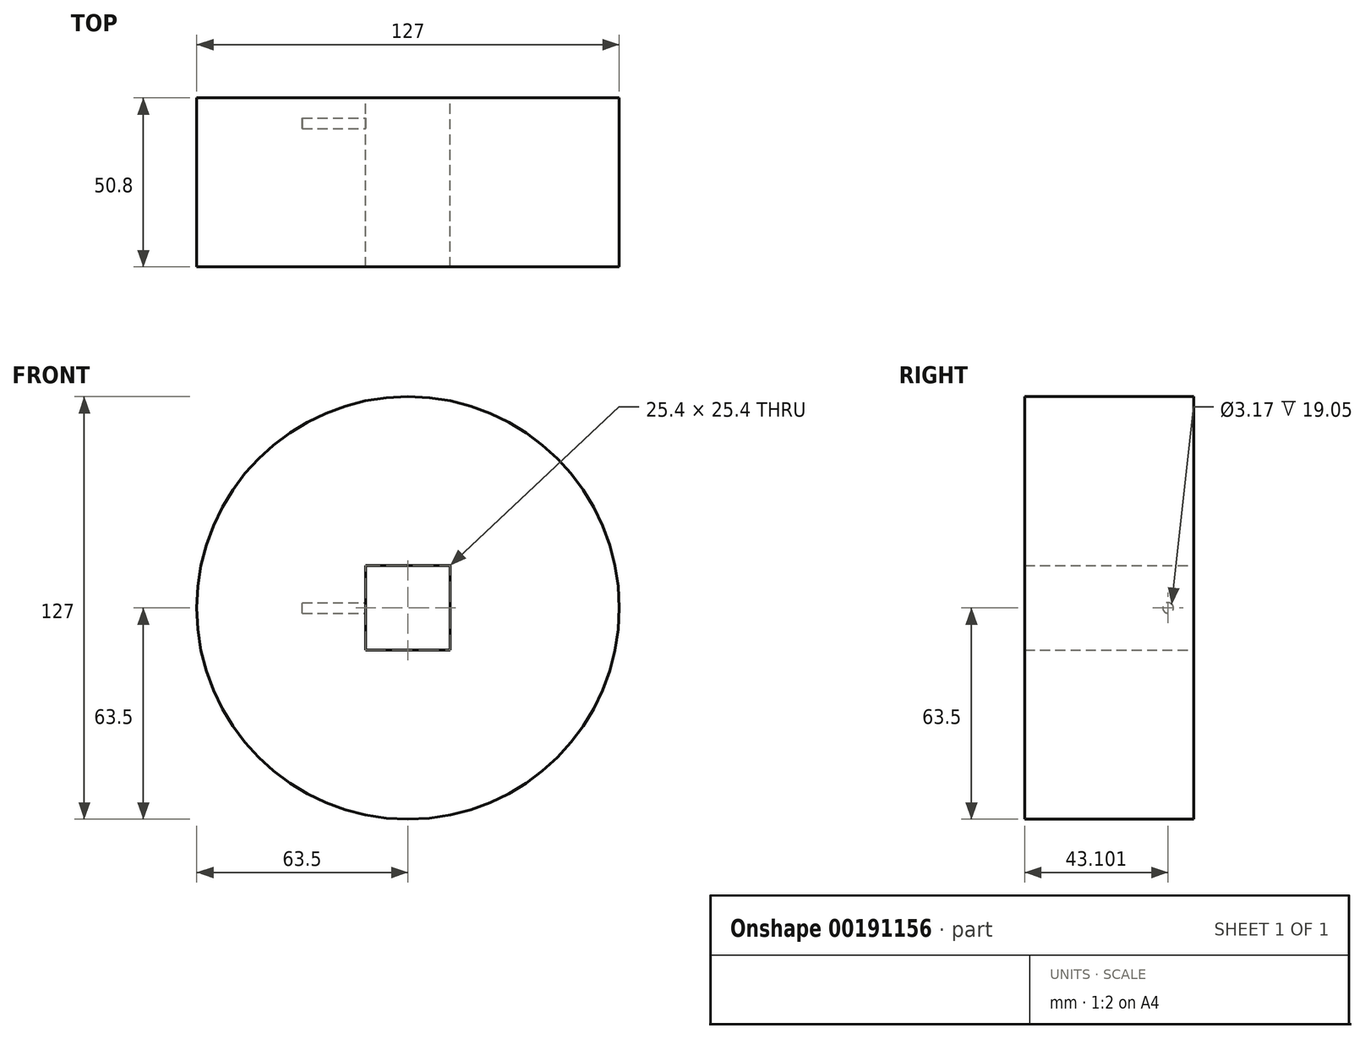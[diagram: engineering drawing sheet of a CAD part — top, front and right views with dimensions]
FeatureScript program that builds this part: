
annotation { "Feature Type Name" : "Feature", "Feature Type Description" : "" }
export const myFeature = defineFeature(function(context is Context, id is Id, definition is map)
    precondition{}
    {
        {
            var Q0;
            Q0=qCreatedBy(makeId("Front.planeOp"),FACE);
            var sketch = newSketch(context, id + "F0", { "sketchPlane" : qUnion([Q0])});
            skCircle(sketch, "E0", {"center": v(0, 0) * mm, "radius": 63.5 * mm});
            skSolve(sketch);
        }
        {
            var Q0;
            Q0=makeQuery(id+"F0.imprint","IMPRINT",FACE,{"disambiguationData":[TD([[makeQuery(id+"F0.imprint","IMPRINT",EDGE,{"derivedFrom":sQuery(id+"F0.wireOp",EDGE,"E0")}),1.0]])]});
            extrude(context, id + "F1", {"entities" : qUnion([Q0]), "depth" : 50.8 * mm});
        }
        {
            var Q0;
            Q0=makeQuery(id+"F1.opExtrude","CAP_FACE",FACE,{"disambiguationData":[OSD([sQuery(id+"F0.wireOp",EDGE,"E0")])],"isStart":true});
            var sketch = newSketch(context, id + "F2", { "sketchPlane" : qUnion([Q0])});
            skLineSegment(sketch, "E1.bottom", {"start": v(-12.7, 12.7) * mm, "end": v(12.7, 12.7) * mm});
            skLineSegment(sketch, "E1.top", {"start": v(-12.7, -12.7) * mm, "end": v(12.7, -12.7) * mm});
            skLineSegment(sketch, "E1.left", {"start": v(-12.7, 12.7) * mm, "end": v(-12.7, -12.7) * mm});
            skLineSegment(sketch, "E1.right", {"start": v(12.7, 12.7) * mm, "end": v(12.7, -12.7) * mm});
            skPoint(sketch, "E1.middle", {"position": v(0, 0) * mm});
            skSolve(sketch);
        }
        {
            var Q0;
            Q0=makeQuery(id+"F2.imprint","IMPRINT",FACE,{"disambiguationData":[TD([[makeQuery(id+"F2.imprint","IMPRINT",EDGE,{"derivedFrom":sQuery(id+"F2.wireOp",EDGE,"E1.bottom")}),-1.0]])]});
            extrude(context, id + "F3", {"entities" : qUnion([Q0]), "operationType" : NewBodyOperationType.REMOVE, "oppositeDirection" : true, "depth" : 50.8 * mm});
        }
        {
            var Q0;
            Q0=qCreatedBy(makeId("Right.planeOp"),FACE);
            var sketch = newSketch(context, id + "F4", { "sketchPlane" : qUnion([Q0])});
            skCircle(sketch, "E2", {"center": v(-7.7, 0) * mm, "radius": 1.59 * mm});
            skSolve(sketch);
        }
        {
            var Q0;
            Q0 = qSketchRegion(id + "F4", true);
            extrude(context, id + "F5", {"entities" : qUnion([Q0]), "operationType" : NewBodyOperationType.REMOVE, "oppositeDirection" : true, "depth" : 31.75 * mm});
        }
    });
